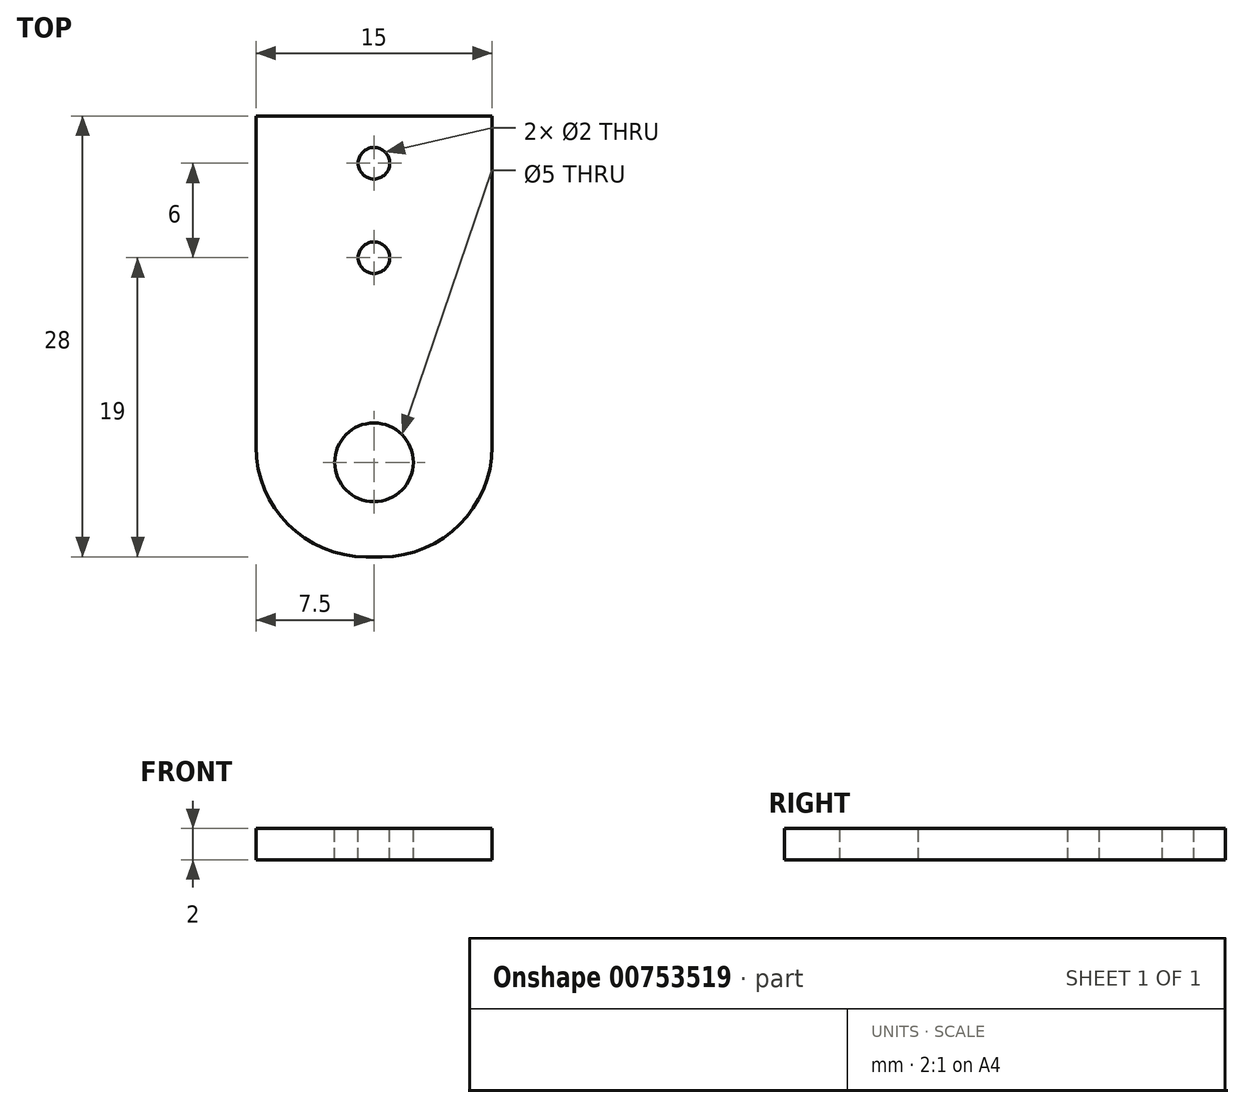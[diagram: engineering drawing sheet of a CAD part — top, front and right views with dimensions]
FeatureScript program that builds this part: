
annotation { "Feature Type Name" : "Feature", "Feature Type Description" : "" }
export const myFeature = defineFeature(function(context is Context, id is Id, definition is map)
    precondition{}
    {
        {
            var Q0;
            Q0=qCreatedBy(makeId("Top.planeOp"),FACE);
            var sketch = newSketch(context, id + "F0", { "sketchPlane" : qUnion([Q0])});
            skLineSegment(sketch, "E0.bottom", {"start": v(-7.5, 14) * mm, "end": v(7.5, 14) * mm});
            skLineSegment(sketch, "E0.top", {"start": v(-7.5, -14) * mm, "end": v(7.5, -14) * mm});
            skLineSegment(sketch, "E0.left", {"start": v(-7.5, 14) * mm, "end": v(-7.5, -14) * mm});
            skLineSegment(sketch, "E0.right", {"start": v(7.5, 14) * mm, "end": v(7.5, -14) * mm});
            skPoint(sketch, "E0.middle", {"position": v(0, 0) * mm});
            skSolve(sketch);
        }
        {
            var Q0;
            Q0 = qSketchRegion(id + "F0", true);
            extrude(context, id + "F1", {"entities" : qUnion([Q0]), "depth" : 2 * mm, "offsetDistance" : 25 * mm});
        }
        {
            var Q0;
            Q0=makeQuery(id+"F1.opExtrude","SWEPT_EDGE",EDGE,{"disambiguationData":[OSD([sQuery(id+"F0.wireOp",EDGE,"E0.top"),sQuery(id+"F0.wireOp",EDGE,"E0.left")])]});
            var Q1;
            Q1=makeQuery(id+"F1.opExtrude","SWEPT_EDGE",EDGE,{"disambiguationData":[OSD([sQuery(id+"F0.wireOp",EDGE,"E0.top"),sQuery(id+"F0.wireOp",EDGE,"E0.right")])]});
            fillet(context, id + "F2", {"entities" : qUnion([Q0, Q1]), "radius" : 7 * mm, "tangentPropagation" : true, "allowEdgeOverflow" : false});
        }
        {
            var Q0;
            Q0=makeQuery(id+"F1.opExtrude","CAP_FACE",FACE,{"disambiguationData":[OSD([sQuery(id+"F0.wireOp",EDGE,"E0.bottom"),sQuery(id+"F0.wireOp",EDGE,"E0.top"),sQuery(id+"F0.wireOp",EDGE,"E0.left"),sQuery(id+"F0.wireOp",EDGE,"E0.right")])],"isStart":false});
            var sketch = newSketch(context, id + "F3", { "sketchPlane" : qUnion([Q0])});
            skCircle(sketch, "E1", {"center": v(0, -8) * mm, "radius": 2.5 * mm});
            skLineSegment(sketch, "E2", {"start": v(0, -14) * mm, "end": v(0, -8) * mm});
            skCircle(sketch, "E3", {"center": v(0, 5) * mm, "radius": 1 * mm});
            skCircle(sketch, "E4", {"center": v(0, 11) * mm, "radius": 1 * mm});
            skSolve(sketch);
        }
        {
            var Q0;
            Q0 = qSketchRegion(id + "F3", true);
            extrude(context, id + "F4", {"entities" : qUnion([Q0]), "operationType" : NewBodyOperationType.REMOVE, "endBound" : BoundingType.UP_TO_NEXT, "oppositeDirection" : true, "depth" : 25 * mm, "offsetDistance" : 25 * mm});
        }
    });
